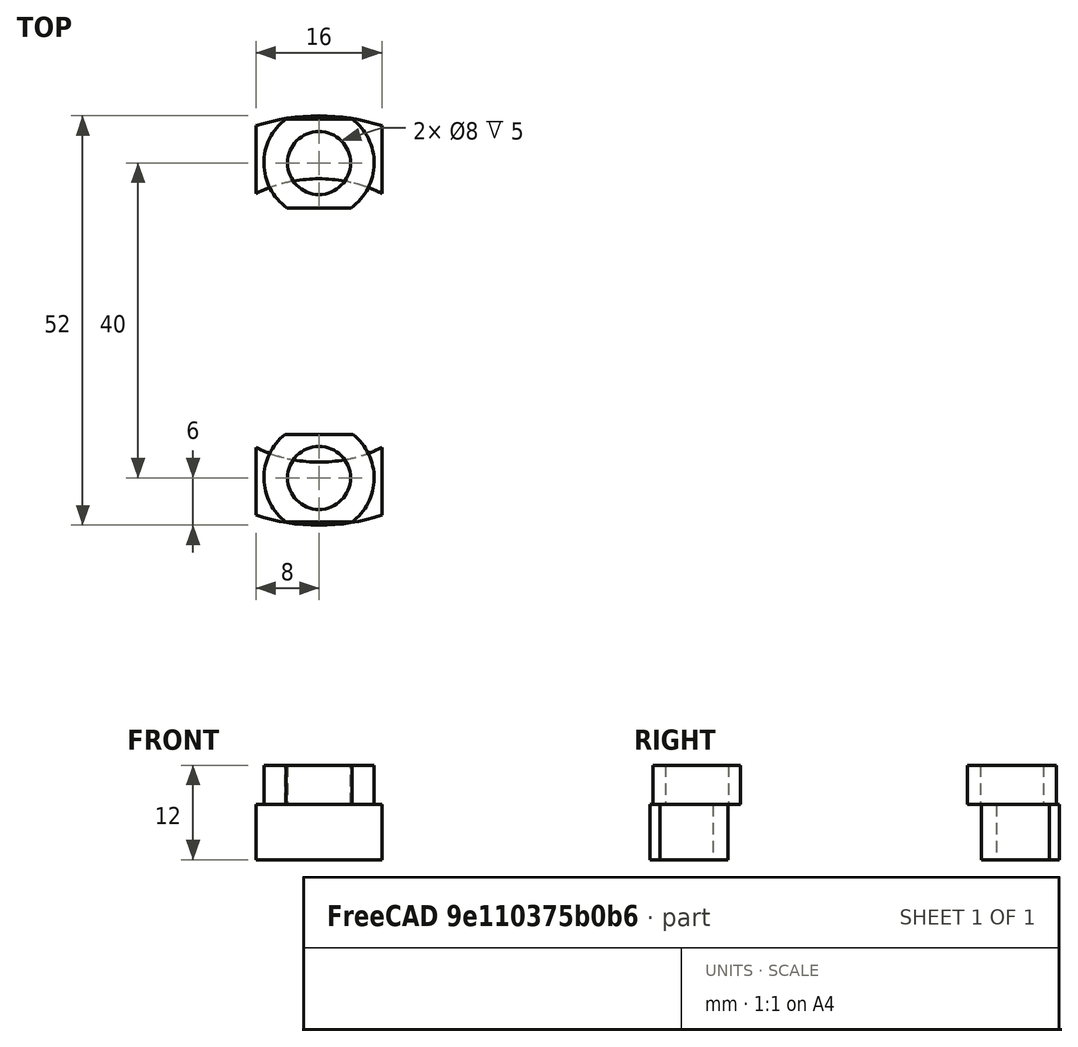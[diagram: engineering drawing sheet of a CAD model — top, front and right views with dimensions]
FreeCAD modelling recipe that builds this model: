
FCSTD DOCUMENT  (FreeCAD 0.21R33668 +26 (Git))
Label: adapted
License: All rights reserved
LicenseURL: https://en.wikipedia.org/wiki/All_rights_reserved
objects: Sketcher::SketchObject×4, PartDesign::Pad×4, PartDesign::Body×2, Mesh::Feature×1
note: 14 computed .brp shape members not serialized (recipe doc carries the construction recipe); baked Part::Feature solids carry a one-line shape summary decoded from their .brp

FEATURE [Mesh::Feature] RollerBall_Fidget
FEATURE [Sketcher::SketchObject] Sketch002
  FullyConstrained = true
  MapMode = 5
  Support = -> [XY_Plane001]
  sketch-geometry (9):
    g0: GeomPoint X=0 Y=-18 Z=0
    g1: GeomPoint X=0 Y=-26 Z=0
    g2: ArcOfCircle CenterX=0 CenterY=0 CenterZ=0 NormalX=0 NormalY=0 NormalZ=1 AngleXU=0 Radius=18 StartAngle=4.25183 EndAngle=5.17294
    g3: ArcOfCircle CenterX=0 CenterY=0 CenterZ=0 NormalX=0 NormalY=0 NormalZ=1 AngleXU=0 Radius=26 StartAngle=4.39962 EndAngle=5.02516
    g4: LineSegment StartX=-8 StartY=-16.1245 StartZ=0 EndX=-8 EndY=-24.7386 EndZ=0
    g5: LineSegment StartX=8 StartY=-16.1245 StartZ=0 EndX=8 EndY=-24.7386 EndZ=0
    g6: GeomPoint X=0 Y=-20 Z=0
    g7: LineSegment StartX=0 StartY=-20 StartZ=0 EndX=-8 EndY=-20 EndZ=0
    g8: LineSegment StartX=0 StartY=-20 StartZ=0 EndX=8 EndY=-20 EndZ=0
  constraints (24):
    c: PointOnObject(g0,g-2)
    c: PointOnObject(g1,g-2)
    c: Distance(g-1,g0) = 18
    c: Distance(g-1,g1) = 26
    c: Coincident(g2,g-1)
    c: Coincident(g3,g2)
    c: PointOnObject(g0,g2)
    c: PointOnObject(g1,g3)
    c: Coincident(g4,g2)
    c: Coincident(g4,g3)
    c: Coincident(g5,g2)
    c: Coincident(g5,g3)
    c: Vertical(g5)
    c: Vertical(g4)
    c: PointOnObject(g6,g-2)
    c: Distance(g6,g0) = 2
    c: Coincident(g7,g6)
    c: PointOnObject(g7,g4)
    c: Coincident(g8,g7)
    c: PointOnObject(g8,g5)
    c: Horizontal(g8)
    c: Horizontal(g7)
    c: Distance(g7) = 8
    c: Distance(g8) = 8
FEATURE [PartDesign::Pad] Pad002
  Direction = (0,0,1)
  Length = 7
  Length2 = 10
  Profile = -> Sketch002
  ReferenceAxis = -> Sketch002 [N_Axis]
  Type = 0
FEATURE [Sketcher::SketchObject] Sketch
  FullyConstrained = true
  MapMode = 5
  Placement = pos=(0,0,7) rot=(0,0,1;0rad)
  Support = -> [Pad002]
  sketch-geometry (10):
    g0: GeomPoint X=0 Y=26 Z=0
    g1: ArcOfCircle CenterX=0 CenterY=0 CenterZ=0 NormalX=0 NormalY=0 NormalZ=1 AngleXU=0 Radius=26 StartAngle=1.25803 EndAngle=1.88356
    g2: GeomPoint X=0 Y=18 Z=0
    g3: ArcOfCircle CenterX=0 CenterY=0 CenterZ=0 NormalX=0 NormalY=0 NormalZ=1 AngleXU=0 Radius=18 StartAngle=1.11024 EndAngle=2.03135
    g4: LineSegment StartX=-8 StartY=24.7386 StartZ=0 EndX=-8 EndY=16.1245 EndZ=0
    g5: LineSegment StartX=8 StartY=24.7386 StartZ=0 EndX=8 EndY=16.1245 EndZ=0
    g6: GeomPoint X=8 Y=20 Z=0
    g7: GeomPoint X=-8 Y=20 Z=0
    g8: LineSegment StartX=8 StartY=20 StartZ=0 EndX=0 EndY=20 EndZ=0
    g9: LineSegment StartX=0 StartY=20 StartZ=0 EndX=-8 EndY=20 EndZ=0
  constraints (25):
    c: PointOnObject(g0,g-2)
    c: Distance(g0,g-1) = 26
    c: Coincident(g1,g-1)
    c: PointOnObject(g0,g1)
    c: PointOnObject(g2,g-2)
    c: Coincident(g3,g1)
    c: PointOnObject(g2,g3)
    c: Distance(g2,g1) = 18
    c: Coincident(g4,g1)
    c: Coincident(g4,g3)
    c: Vertical(g4)
    c: Coincident(g5,g1)
    c: Coincident(g5,g3)
    c: Vertical(g5)
    c: PointOnObject(g6,g5)
    c: PointOnObject(g7,g4)
    c: Coincident(g8,g6)
    c: PointOnObject(g8,g-2)
    c: Horizontal(g8)
    c: Coincident(g9,g8)
    c: Coincident(g9,g7)
    c: Horizontal(g9)
    c: Distance(g9) = 8
    c: Distance(g8) = 8
    c: Distance(g8,g2) = 2
FEATURE [PartDesign::Pad] Pad
  Direction = (0,0,1)
  Length = 7
  Length2 = 10
  Profile = -> Sketch
  ReferenceAxis = -> Sketch [N_Axis]
  Type = 0
FEATURE [Sketcher::SketchObject] Sketch001
  FullyConstrained = false
  MapMode = 5
  Placement = pos=(0,0,7) rot=(0,0,1;0rad)
  Support = -> [Pad]
  sketch-geometry (9):
    g0: GeomPoint X=0 Y=20 Z=0
    g1: Circle CenterX=0 CenterY=20 CenterZ=0 NormalX=0 NormalY=0 NormalZ=1 AngleXU=0 Radius=4
    g2: GeomPoint X=1.05876 Y=23.8573 Z=0
    g3: ArcOfCircle CenterX=0 CenterY=20 CenterZ=0 NormalX=0 NormalY=0 NormalZ=1 AngleXU=0 Radius=7 StartAngle=2.21404 EndAngle=4.0907
    g4: ArcOfCircle CenterX=0 CenterY=20 CenterZ=0 NormalX=0 NormalY=0 NormalZ=1 AngleXU=0 Radius=7 StartAngle=5.33407 EndAngle=7.21074
    g5: LineSegment StartX=-4.19857 StartY=25.6011 StartZ=0 EndX=4.19857 EndY=25.6011 EndZ=0
    g6: LineSegment StartX=-4.07685 StartY=14.3097 StartZ=0 EndX=4.07685 EndY=14.3097 EndZ=0
    g7: GeomPoint X=6.91834 Y=21.0661 Z=0
    g8: GeomPoint X=-6.92339 Y=21.0328 Z=0
  constraints (17):
    c: PointOnObject(g0,g-2)
    c: Distance(g-1,g0) = 20
    c: Coincident(g1,g0)
    c: PointOnObject(g2,g1)
    c: Distance(g1,g2) = 4
    c: Coincident(g3,g0)
    c: Coincident(g4,g3)
    c: Coincident(g5,g3)
    c: Coincident(g5,g4)
    c: Horizontal(g5)
    c: Coincident(g6,g3)
    c: Coincident(g6,g4)
    c: Horizontal(g6)
    c: PointOnObject(g7,g4)
    c: PointOnObject(g8,g3)
    c: Distance(g8,g3) = 7
    c: Distance(g3,g7) = 7
FEATURE [PartDesign::Pad] Pad001
  BaseFeature = -> Pad
  Direction = (0,0,1)
  Length = 5
  Length2 = 10
  Profile = -> Sketch001
  ReferenceAxis = -> Sketch001 [N_Axis]
  Type = 0
FEATURE [PartDesign::Body] Body
  Group = -> [Sketch,Pad,Sketch001,Pad001]
  Origin = -> Origin
  Tip = -> Pad001
FEATURE [Sketcher::SketchObject] Sketch003
  FullyConstrained = false
  MapMode = 5
  Placement = pos=(0,0,7) rot=(0,0,1;0rad)
  Support = -> [Pad002]
  sketch-geometry (9):
    g0: GeomPoint X=0 Y=-20 Z=0
    g1: Circle CenterX=0 CenterY=-20 CenterZ=0 NormalX=0 NormalY=0 NormalZ=1 AngleXU=0 Radius=4
    g2: GeomPoint X=2.03036 Y=-16.5536 Z=0
    g3: ArcOfCircle CenterX=0 CenterY=-20 CenterZ=0 NormalX=0 NormalY=0 NormalZ=1 AngleXU=0 Radius=7 StartAngle=5.35038 EndAngle=7.19062
    g4: ArcOfCircle CenterX=0 CenterY=-20 CenterZ=0 NormalX=0 NormalY=0 NormalZ=1 AngleXU=0 Radius=7 StartAngle=2.23416 EndAngle=4.0744
    g5: LineSegment StartX=-4.31037 StartY=-14.4845 StartZ=0 EndX=4.31037 EndY=-14.4845 EndZ=0
    g6: LineSegment StartX=-4.16907 StartY=-25.6231 StartZ=0 EndX=4.16907 EndY=-25.6231 EndZ=0
    g7: GeomPoint X=-6.99717 Y=-19.801 Z=0
    g8: GeomPoint X=6.99974 Y=-20.0608 Z=0
  constraints (17):
    c: PointOnObject(g0,g-2)
    c: Coincident(g1,g0)
    c: PointOnObject(g2,g1)
    c: Distance(g1,g2) = 4
    c: Distance(g1,g-1) = 20
    c: Coincident(g3,g1)
    c: Coincident(g4,g1)
    c: Coincident(g5,g4)
    c: Coincident(g5,g3)
    c: Coincident(g6,g4)
    c: Coincident(g6,g3)
    c: Horizontal(g6)
    c: Horizontal(g5)
    c: PointOnObject(g7,g4)
    c: PointOnObject(g8,g3)
    c: Distance(g1,g8) = 7
    c: Distance(g7,g1) = 7
FEATURE [PartDesign::Pad] Pad003
  BaseFeature = -> Pad002
  Direction = (0,0,1)
  Length = 5
  Length2 = 10
  Profile = -> Sketch003
  ReferenceAxis = -> Sketch003 [N_Axis]
  Type = 0
FEATURE [PartDesign::Body] Body001  label="Körper"
  Group = -> [Sketch002,Pad002,Sketch003,Pad003]
  Origin = -> Origin001
  Tip = -> Pad003
